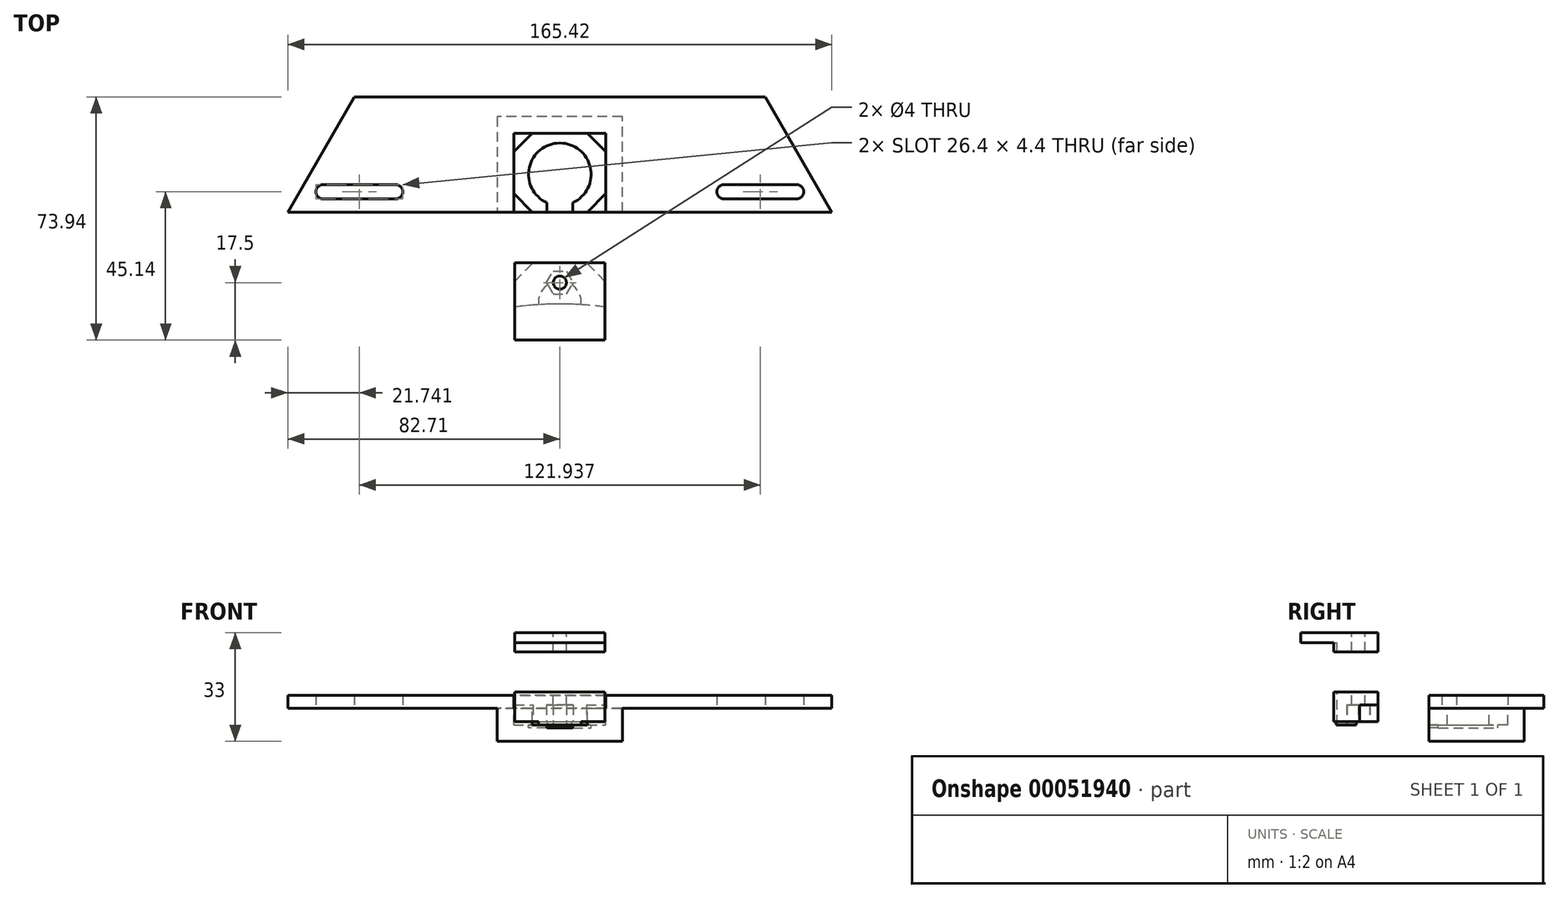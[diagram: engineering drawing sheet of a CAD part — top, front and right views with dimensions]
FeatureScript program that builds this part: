
annotation { "Feature Type Name" : "Feature", "Feature Type Description" : "" }
export const myFeature = defineFeature(function(context is Context, id is Id, definition is map)
    precondition{}
    {
        {
            var Q0;
            Q0=qCreatedBy(makeId("Top.planeOp"),FACE);
            var sketch = newSketch(context, id + "F0", { "sketchPlane" : qUnion([Q0])});
            skLineSegment(sketch, "E0.bottom", {"start": v(-62.5, 35) * mm, "end": v(-14, 35) * mm});
            skLineSegment(sketch, "E0.top", {"start": v(-62.5, 0) * mm, "end": v(-14, 0) * mm});
            skLineSegment(sketch, "E0.left", {"start": v(-62.5, 35) * mm, "end": v(-62.5, 0) * mm, "construction": true});
            skLineSegment(sketch, "E1", {"start": v(-62.5, 35) * mm, "end": v(-82.7, 0) * mm});
            skLineSegment(sketch, "E2", {"start": v(-82.7, 0) * mm, "end": v(-62.5, 0) * mm});
            skLineSegment(sketch, "E3", {"start": v(-14, 24) * mm, "end": v(-14, 0) * mm});
            skArc(sketch, "E4", {"start": v(-49.97, 4) * mm, "mid": v(-47.77, 6.2) * mm, "end": v(-49.97, 8.4) * mm});
            skLineSegment(sketch, "E5", {"start": v(-49.97, 8.4) * mm, "end": v(-71.97, 8.4) * mm});
            skLineSegment(sketch, "E6", {"start": v(-49.97, 4) * mm, "end": v(-71.97, 4) * mm});
            skArc(sketch, "E7", {"start": v(-71.97, 8.4) * mm, "mid": v(-74.17, 6.2) * mm, "end": v(-71.97, 4) * mm});
            skLineSegment(sketch, "E8", {"start": v(-14, 35) * mm, "end": v(0, 35) * mm});
            skLineSegment(sketch, "E9", {"start": v(0, 35) * mm, "end": v(0, 24) * mm});
            skLineSegment(sketch, "E10", {"start": v(0, 24) * mm, "end": v(-14, 24) * mm});
            skLineSegment(sketch, "E11.MirrorCS", {"start": v(62.5, 35) * mm, "end": v(82.7, 0) * mm});
            skArc(sketch, "E12.MirrorCS", {"start": v(49.97, 4) * mm, "mid": v(47.77, 6.2) * mm, "end": v(49.97, 8.4) * mm});
            skLineSegment(sketch, "E13.MirrorCS", {"start": v(0, 24) * mm, "end": v(14, 24) * mm});
            skLineSegment(sketch, "E14.MirrorCS", {"start": v(62.5, 35) * mm, "end": v(14, 35) * mm});
            skLineSegment(sketch, "E15.MirrorCS", {"start": v(62.5, 0) * mm, "end": v(14, 0) * mm});
            skLineSegment(sketch, "E16.MirrorCS", {"start": v(62.5, 35) * mm, "end": v(62.5, 0) * mm, "construction": true});
            skLineSegment(sketch, "E17.MirrorCS", {"start": v(82.7, 0) * mm, "end": v(62.5, 0) * mm});
            skLineSegment(sketch, "E18.MirrorCS", {"start": v(14, 24) * mm, "end": v(14, 0) * mm});
            skArc(sketch, "E19.MirrorCS", {"start": v(71.97, 8.4) * mm, "mid": v(74.17, 6.2) * mm, "end": v(71.97, 4) * mm});
            skLineSegment(sketch, "E20.MirrorCS", {"start": v(49.97, 8.4) * mm, "end": v(71.97, 8.4) * mm});
            skLineSegment(sketch, "E21.MirrorCS", {"start": v(49.97, 4) * mm, "end": v(71.97, 4) * mm});
            skLineSegment(sketch, "E22.MirrorCS", {"start": v(14, 35) * mm, "end": v(0, 35) * mm});
            skSolve(sketch);
        }
        {
            var Q0;
            Q0 = qSketchRegion(id + "F0", true);
            extrude(context, id + "F1", {"entities" : qUnion([Q0]), "depth" : 4 * mm});
        }
        {
            var Q0;
            Q0=makeQuery(id+"F1.opExtrude","CAP_FACE",FACE,{"disambiguationData":[OSD([sQuery(id+"F0.wireOp",EDGE,"E0.bottom"),sQuery(id+"F0.wireOp",EDGE,"E0.top"),sQuery(id+"F0.wireOp",EDGE,"E1"),sQuery(id+"F0.wireOp",EDGE,"E2"),sQuery(id+"F0.wireOp",EDGE,"E3"),sQuery(id+"F0.wireOp",EDGE,"E4"),sQuery(id+"F0.wireOp",EDGE,"E5"),sQuery(id+"F0.wireOp",EDGE,"E6"),sQuery(id+"F0.wireOp",EDGE,"E7"),sQuery(id+"F0.wireOp",EDGE,"E8"),sQuery(id+"F0.wireOp",EDGE,"E10"),sQuery(id+"F0.wireOp",EDGE,"E11.MirrorCS"),sQuery(id+"F0.wireOp",EDGE,"E12.MirrorCS"),sQuery(id+"F0.wireOp",EDGE,"E13.MirrorCS"),sQuery(id+"F0.wireOp",EDGE,"E14.MirrorCS"),sQuery(id+"F0.wireOp",EDGE,"E15.MirrorCS"),sQuery(id+"F0.wireOp",EDGE,"E17.MirrorCS"),sQuery(id+"F0.wireOp",EDGE,"E18.MirrorCS"),sQuery(id+"F0.wireOp",EDGE,"E19.MirrorCS"),sQuery(id+"F0.wireOp",EDGE,"E20.MirrorCS"),sQuery(id+"F0.wireOp",EDGE,"E21.MirrorCS"),sQuery(id+"F0.wireOp",EDGE,"E22.MirrorCS")])],"isStart":true});
            var sketch = newSketch(context, id + "F2", { "sketchPlane" : qUnion([Q0])});
            skLineSegment(sketch, "E23", {"start": v(19, 0) * mm, "end": v(19, -29) * mm});
            skLineSegment(sketch, "E24", {"start": v(19, -29) * mm, "end": v(-19, -29) * mm});
            skLineSegment(sketch, "E25", {"start": v(-19, -29) * mm, "end": v(-19, 0) * mm});
            skLineSegment(sketch, "E26", {"start": v(-19, 0) * mm, "end": v(-14, 0) * mm});
            skLineSegment(sketch, "E27", {"start": v(-14, -5.66) * mm, "end": v(-14, -18.34) * mm});
            skLineSegment(sketch, "E28", {"start": v(-8.34, -24) * mm, "end": v(8.34, -24) * mm});
            skLineSegment(sketch, "E29", {"start": v(14, -18.34) * mm, "end": v(14, -5.66) * mm});
            skLineSegment(sketch, "E30", {"start": v(14, 0) * mm, "end": v(19, 0) * mm});
            skLineSegment(sketch, "E31", {"start": v(14, -5.66) * mm, "end": v(8.34, 0) * mm});
            skLineSegment(sketch, "E32", {"start": v(14, -18.34) * mm, "end": v(8.34, -24) * mm});
            skLineSegment(sketch, "E33", {"start": v(-8.34, -24) * mm, "end": v(-14, -18.34) * mm});
            skLineSegment(sketch, "E34", {"start": v(-14, -5.66) * mm, "end": v(-8.34, 0) * mm});
            skLineSegment(sketch, "E35", {"start": v(8.34, 0) * mm, "end": v(14, 0) * mm});
            skLineSegment(sketch, "E36", {"start": v(-8.34, 0) * mm, "end": v(-14, 0) * mm});
            skSolve(sketch);
        }
        {
            var Q0;
            Q0 = qSketchRegion(id + "F2", true);
            extrude(context, id + "F3", {"entities" : qUnion([Q0]), "operationType" : NewBodyOperationType.ADD, "depth" : 10 * mm});
        }
        {
            var Q0;
            Q0=qCreatedBy(makeId("Top.planeOp"),FACE);
            cPlane(context, id + "F4", {"entities" : qUnion([Q0]), "cplaneType" : CPlaneType.OFFSET, "offset" : 5 * mm, "oppositeDirection" : true, "width" : 150 * mm, "height" : 150 * mm});
        }
        {
            var Q0;
            Q0=qCreatedBy(id+"F4.planeOp",FACE);
            var sketch = newSketch(context, id + "F5", { "sketchPlane" : qUnion([Q0])});
            skCircle(sketch, "E37", {"center": v(0, 11.5) * mm, "radius": 9.5 * mm});
            skLineSegment(sketch, "E38", {"start": v(-4, 2.88) * mm, "end": v(-4, 0) * mm});
            skLineSegment(sketch, "E39", {"start": v(-4, 0) * mm, "end": v(4, 0) * mm});
            skLineSegment(sketch, "E40", {"start": v(4, 0) * mm, "end": v(4, 2.88) * mm});
            skSolve(sketch);
        }
        {
            var Q0;
            Q0=qCreatedBy(id+"F4.planeOp",FACE);
            var sketch = newSketch(context, id + "F6", { "sketchPlane" : qUnion([Q0])});
            skLineSegment(sketch, "E41", {"start": v(-14, 0) * mm, "end": v(-14, 24) * mm});
            skLineSegment(sketch, "E42", {"start": v(-14, 24) * mm, "end": v(14, 24) * mm});
            skLineSegment(sketch, "E43", {"start": v(14, 24) * mm, "end": v(14, 0) * mm});
            skLineSegment(sketch, "E44", {"start": v(14, 0) * mm, "end": v(-14, 0) * mm});
            skSolve(sketch);
        }
        {
            var Q0;
            Q0=makeQuery(id+"F6.imprint","IMPRINT",FACE,{"disambiguationData":[TD([[makeQuery(id+"F6.imprint","IMPRINT",EDGE,{"derivedFrom":sQuery(id+"F6.wireOp",EDGE,"E41")}),-1.0]])]});
            extrude(context, id + "F7", {"entities" : qUnion([Q0]), "operationType" : NewBodyOperationType.ADD, "oppositeDirection" : true, "depth" : 5 * mm});
        }
        {
            var Q0;
            Q0 = qSketchRegion(id + "F5", true);
            extrude(context, id + "F8", {"entities" : qUnion([Q0]), "operationType" : NewBodyOperationType.REMOVE, "oppositeDirection" : true, "depth" : 1 * mm});
        }
        {
            var Q0;
            Q0=qCreatedBy(makeId("Top.planeOp"),FACE);
            var sketch = newSketch(context, id + "F9", { "sketchPlane" : qUnion([Q0])});
            skLineSegment(sketch, "E45.bottom", {"start": v(-13.75, -15.44) * mm, "end": v(13.75, -15.44) * mm});
            skLineSegment(sketch, "E45.top", {"start": v(-13.75, -38.94) * mm, "end": v(13.75, -38.94) * mm});
            skLineSegment(sketch, "E45.left", {"start": v(-13.75, -15.44) * mm, "end": v(-13.75, -38.94) * mm});
            skLineSegment(sketch, "E45.right", {"start": v(13.75, -15.44) * mm, "end": v(13.75, -38.94) * mm});
            skPoint(sketch, "E46", {"position": v(0, -15.44) * mm});
            skSolve(sketch);
        }
        {
            var Q0;
            Q0 = qSketchRegion(id + "F9", true);
            extrude(context, id + "F10", {"entities" : qUnion([Q0]), "depth" : 5 * mm, "hasSecondDirection" : true, "secondDirectionOppositeDirection" : true, "secondDirectionDepth" : 4 * mm});
        }
        {
            var Q0;
            Q0=makeQuery(id+"F10.opExtrude","CAP_FACE",FACE,{"disambiguationData":[OSD([sQuery(id+"F9.wireOp",EDGE,"E45.bottom"),sQuery(id+"F9.wireOp",EDGE,"E45.top"),sQuery(id+"F9.wireOp",EDGE,"E45.left"),sQuery(id+"F9.wireOp",EDGE,"E45.right")])],"isStart":true});
            var sketch = newSketch(context, id + "F11", { "sketchPlane" : qUnion([Q0])});
            skCircle(sketch, "E47", {"center": v(0, 27.44) * mm, "radius": 6.5 * mm});
            skSolve(sketch);
        }
        {
            var Q0;
            Q0 = qSketchRegion(id + "F11", true);
            extrude(context, id + "F12", {"entities" : qUnion([Q0]), "operationType" : NewBodyOperationType.ADD, "depth" : 1 * mm});
        }
        {
            var Q0;
            Q0=makeQuery(id+"F10.opExtrude","CAP_FACE",FACE,{"disambiguationData":[OSD([sQuery(id+"F9.wireOp",EDGE,"E45.bottom"),sQuery(id+"F9.wireOp",EDGE,"E45.top"),sQuery(id+"F9.wireOp",EDGE,"E45.left"),sQuery(id+"F9.wireOp",EDGE,"E45.right")])],"isStart":true});
            var sketch = newSketch(context, id + "F13", { "sketchPlane" : qUnion([Q0])});
            skLineSegment(sketch, "E48", {"start": v(13.75, 15.44) * mm, "end": v(13.75, 21.1) * mm});
            skLineSegment(sketch, "E49", {"start": v(13.75, 21.1) * mm, "end": v(8.1, 15.44) * mm});
            skLineSegment(sketch, "E50", {"start": v(8.1, 15.44) * mm, "end": v(13.75, 15.44) * mm});
            skLineSegment(sketch, "E51", {"start": v(13.75, 33.28) * mm, "end": v(8.1, 38.94) * mm});
            skLineSegment(sketch, "E52", {"start": v(8.1, 38.94) * mm, "end": v(13.75, 38.94) * mm});
            skLineSegment(sketch, "E53", {"start": v(13.75, 38.94) * mm, "end": v(13.75, 33.28) * mm});
            skLineSegment(sketch, "E54.MirrorCS", {"start": v(-8.1, 38.94) * mm, "end": v(-13.75, 38.94) * mm});
            skLineSegment(sketch, "E55.MirrorCS", {"start": v(-13.75, 15.44) * mm, "end": v(-13.75, 21.1) * mm});
            skLineSegment(sketch, "E56.MirrorCS", {"start": v(-13.75, 38.94) * mm, "end": v(-13.75, 33.28) * mm});
            skLineSegment(sketch, "E57.MirrorCS", {"start": v(-13.75, 33.28) * mm, "end": v(-8.1, 38.94) * mm});
            skLineSegment(sketch, "E58.MirrorCS", {"start": v(-8.1, 15.44) * mm, "end": v(-13.75, 15.44) * mm});
            skLineSegment(sketch, "E59.MirrorCS", {"start": v(-13.75, 21.1) * mm, "end": v(-8.1, 15.44) * mm});
            skSolve(sketch);
        }
        {
            var Q0;
            Q0 = qSketchRegion(id + "F13", true);
            extrude(context, id + "F14", {"entities" : qUnion([Q0]), "operationType" : NewBodyOperationType.REMOVE, "oppositeDirection" : true, "depth" : 5 * mm});
        }
        {
            var Q0;
            Q0=makeQuery(id+"F10.opExtrude","CAP_FACE",FACE,{"disambiguationData":[OSD([sQuery(id+"F9.wireOp",EDGE,"E45.bottom"),sQuery(id+"F9.wireOp",EDGE,"E45.top"),sQuery(id+"F9.wireOp",EDGE,"E45.left"),sQuery(id+"F9.wireOp",EDGE,"E45.right")])],"isStart":false});
            cPlane(context, id + "F15", {"entities" : qUnion([Q0]), "cplaneType" : CPlaneType.OFFSET, "offset" : 15 * mm, "width" : 150 * mm, "height" : 150 * mm});
        }
        {
            var Q0;
            Q0=qCreatedBy(id+"F15.planeOp",FACE);
            var sketch = newSketch(context, id + "F16", { "sketchPlane" : qUnion([Q0])});
            skLineSegment(sketch, "E60.bottom", {"start": v(-13.75, -15.44) * mm, "end": v(13.75, -15.44) * mm});
            skLineSegment(sketch, "E60.top", {"start": v(-13.75, -38.94) * mm, "end": v(13.75, -38.94) * mm});
            skLineSegment(sketch, "E60.left", {"start": v(-13.75, -15.44) * mm, "end": v(-13.75, -38.94) * mm});
            skLineSegment(sketch, "E60.right", {"start": v(13.75, -15.44) * mm, "end": v(13.75, -38.94) * mm});
            skPoint(sketch, "E61", {"position": v(0, -15.44) * mm});
            skSolve(sketch);
        }
        {
            var Q0;
            Q0 = qSketchRegion(id + "F16", true);
            extrude(context, id + "F17", {"entities" : qUnion([Q0]), "depth" : 3 * mm, "hasSecondDirection" : true, "secondDirectionOppositeDirection" : true, "secondDirectionDepth" : 2.8 * mm});
        }
        {
            var Q0;
            Q0=makeQuery(id+"F17.opExtrude","CAP_FACE",FACE,{"disambiguationData":[OSD([sQuery(id+"F16.wireOp",EDGE,"E60.bottom"),sQuery(id+"F16.wireOp",EDGE,"E60.top"),sQuery(id+"F16.wireOp",EDGE,"E60.left"),sQuery(id+"F16.wireOp",EDGE,"E60.right")])],"isStart":false});
            var sketch = newSketch(context, id + "F18", { "sketchPlane" : qUnion([Q0])});
            skCircle(sketch, "E62", {"center": v(0, -21.44) * mm, "radius": 2 * mm});
            skSolve(sketch);
        }
        {
            var Q0;
            Q0 = qSketchRegion(id + "F18", true);
            extrude(context, id + "F19", {"entities" : qUnion([Q0]), "operationType" : NewBodyOperationType.REMOVE, "oppositeDirection" : true, "depth" : 50 * mm});
        }
        {
            var Q0;
            Q0=makeQuery(id+"F10.opExtrude","CAP_FACE",FACE,{"disambiguationData":[OSD([sQuery(id+"F9.wireOp",EDGE,"E45.bottom"),sQuery(id+"F9.wireOp",EDGE,"E45.top"),sQuery(id+"F9.wireOp",EDGE,"E45.left"),sQuery(id+"F9.wireOp",EDGE,"E45.right")])],"isStart":true});
            var sketch = newSketch(context, id + "F20", { "sketchPlane" : qUnion([Q0])});
            skCircle(sketch, "E63.cCircle", {"center": v(0, 21.44) * mm, "radius": 3.5 * mm, "construction": true});
            skLineSegment(sketch, "E63.0", {"start": v(-4.04, 21.4) * mm, "end": v(-2.05, 24.92) * mm});
            skLineSegment(sketch, "E63.1", {"start": v(-2.05, 24.92) * mm, "end": v(2, 24.96) * mm});
            skLineSegment(sketch, "E63.2", {"start": v(2, 24.96) * mm, "end": v(4.04, 21.47) * mm});
            skLineSegment(sketch, "E63.3", {"start": v(4.04, 21.47) * mm, "end": v(2.05, 17.96) * mm});
            skLineSegment(sketch, "E63.4", {"start": v(2.05, 17.96) * mm, "end": v(-2, 17.92) * mm});
            skLineSegment(sketch, "E63.5", {"start": v(-2, 17.92) * mm, "end": v(-4.04, 21.4) * mm});
            skPoint(sketch, "E63.0.midPoint", {"position": v(-3.05, 23.16) * mm});
            skSolve(sketch);
        }
        {
            var Q0;
            Q0 = qSketchRegion(id + "F20", true);
            extrude(context, id + "F21", {"entities" : qUnion([Q0]), "operationType" : NewBodyOperationType.REMOVE, "oppositeDirection" : true, "depth" : 5 * mm, "hasSecondDirection" : true, "secondDirectionOppositeDirection" : false, "secondDirectionDepth" : 2 * mm});
        }
        {
            var Q0;
            Q0=qCreatedBy(id+"F15.planeOp",FACE);
            var sketch = newSketch(context, id + "F22", { "sketchPlane" : qUnion([Q0])});
            skArc(sketch, "E64", {"start": v(42.45, -37.4) * mm, "mid": v(3.06, -27.99) * mm, "end": v(-36.84, -34.97) * mm});
            skLineSegment(sketch, "E65", {"start": v(-36.84, -34.97) * mm, "end": v(-14.82, -51.81) * mm});
            skLineSegment(sketch, "E66", {"start": v(-14.82, -51.81) * mm, "end": v(34.04, -52.06) * mm});
            skLineSegment(sketch, "E67", {"start": v(34.04, -52.06) * mm, "end": v(42.45, -37.4) * mm});
            skSolve(sketch);
        }
        {
            var Q0;
            Q0 = qSketchRegion(id + "F22", true);
            extrude(context, id + "F23", {"entities" : qUnion([Q0]), "operationType" : NewBodyOperationType.REMOVE, "oppositeDirection" : true, "depth" : 25 * mm});
        }
    });
